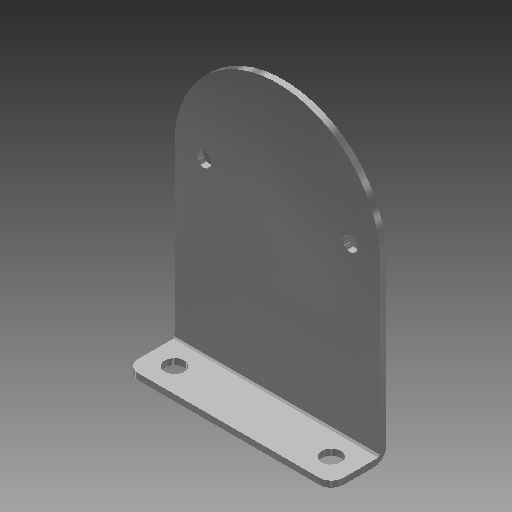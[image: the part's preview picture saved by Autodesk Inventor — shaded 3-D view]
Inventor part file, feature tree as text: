
AUTODESK INVENTOR PART (.ipt)
format: ipt  version: 2018.2 (Build 222227000, 227)  size: 137,728 bytes
history: native  units: in
note: dims shown in document units (in); Inventor stores cm internally (conversion verified against a paired STEP export)
features: fillet x3, hole x3, sketch x3, extrude x2, reference x2
ambient origin geometry x8: Origin, YZ Plane, XZ Plane, XY Plane, X Axis, Y Axis, Z Axis, Center Point
bodies: Solid1 (feature_tree)
feature tree (13):
  extrude  "Extrusion1"  Depth=0.0625in
  extrude  "Extrusion2"  Depth=0.125in
  fillet  "Fillet1"  Radius=0.0312in
  hole  "Hole1"  [1 undecoded]
  fillet  "Fillet2"  Radius=0.75in
  hole  "Hole2"  [1 undecoded]
  hole  "Hole3"  [1 undecoded]
  fillet  "Fillet3"  [1 undecoded]
  sketch  "Sketch1"  dims[d0=0.0625in d1=0.0in d2=0.0625in]
  reference  "Reference1"
  sketch  "Sketch2"  dims[d3=0.5in d4=0.0in d5=0.125in]
  sketch  "Sketch3"  dims[d6=0.25in d16=0.25in d8=0.201in d9=0.75in d10=0.385in d11=0.25in d12=0.5635in d13=1.0in d14=0.8108in d15=0.0312in d17=0.25in d18=0.25in d19=0.201in d20=0.75in d21=0.385in d22=0.25in d23=0.5635in d24=1.0in d25=0.8108in d26=0.75in d27=0.75in d28=0.15in d29=0.75in d30=0.385in d31=0.25in d32=0.5635in d33=1.0in d34=0.8108in d35=0.125in]
  reference  "Reference3"
note: 4 required parameter values undecoded (feature->parameter linkage not recoverable at this tier; creation-order binding heuristic only, values carry confidence <= 0.55)
